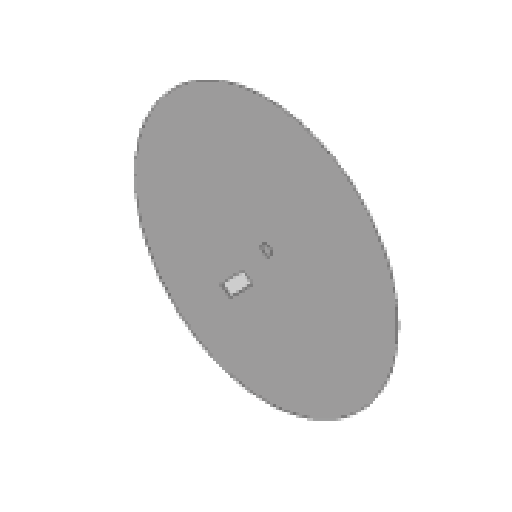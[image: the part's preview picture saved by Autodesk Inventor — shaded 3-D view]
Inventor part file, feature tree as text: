
AUTODESK INVENTOR PART (.ipt)
format: ipt  version: 2023 (Build 270158000, 158)  size: 110,592 bytes
history: native  units: in
note: dims shown in document units (in); Inventor stores cm internally (conversion verified against a paired STEP export)
features: extrude x4, sketch x4, projected_geometry x3
ambient origin geometry x8: Origin, YZ Plane, XZ Plane, XY Plane, X Axis, Y Axis, Z Axis, Center Point
bodies: Solid1 (feature_tree)
feature tree (11):
  extrude  "Extrusion1"  Depth=1.0in
  extrude  "Extrusion2"  Depth=78.7402in TaperAngle=0.0deg
  extrude  "Extrusion3"  Depth=1.0in
  extrude  "Extrusion4"  [1 undecoded]
  sketch  "Sketch1"  dims[d0=1.0in d1=0.0in d2=39.3701in]
  sketch  "Sketch2"  dims[d3=0.01in d4=0.0in d5=78.7402in d6=0.0in]
  projected_geometry  "Projected Loop1"
  sketch  "Sketch3"  dims[d7=1.0in d8=984.252in]
  projected_geometry  "Projected Loop2"
  sketch  "Sketch4"  dims[d9=7.874in d10=0.0in]
  projected_geometry  "Projected Loop3"
note: 1 required parameter value undecoded (feature->parameter linkage not recoverable at this tier; creation-order binding heuristic only, values carry confidence <= 0.55)
